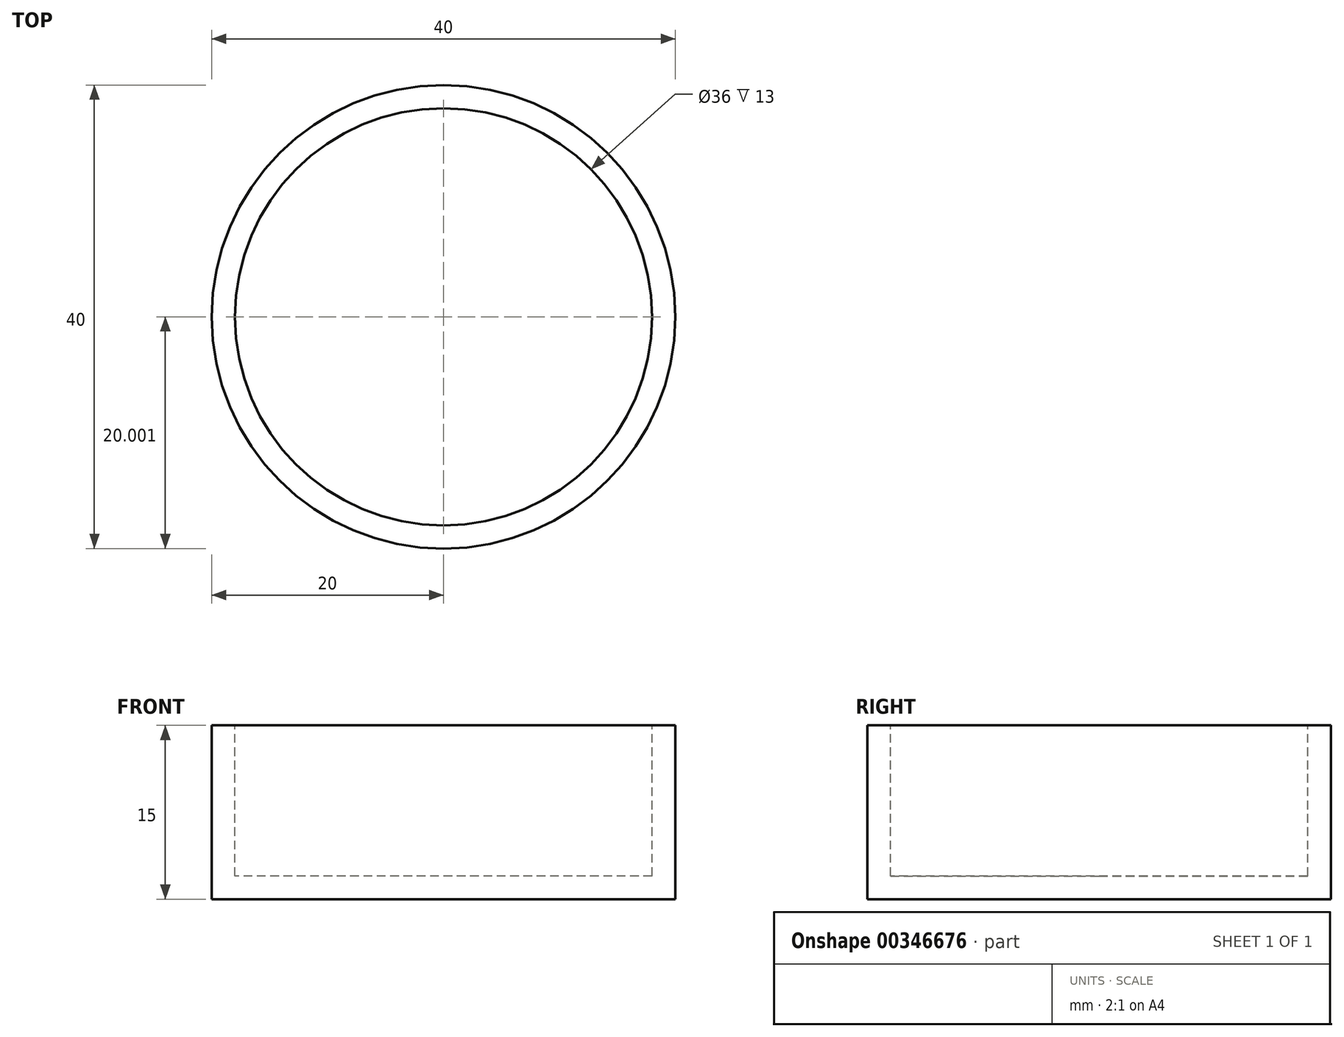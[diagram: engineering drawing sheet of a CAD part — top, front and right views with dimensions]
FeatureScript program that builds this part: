
annotation { "Feature Type Name" : "Feature", "Feature Type Description" : "" }
export const myFeature = defineFeature(function(context is Context, id is Id, definition is map)
    precondition{}
    {
        {
            var Q0;
            Q0=qCreatedBy(makeId("Top.planeOp"),FACE);
            var sketch = newSketch(context, id + "F0", { "sketchPlane" : qUnion([Q0])});
            skCircle(sketch, "E0", {"center": v(0, -2.77) * mm, "radius": 20 * mm});
            skSolve(sketch);
        }
        {
            var Q0;
            Q0=makeQuery(id+"F0.imprint","IMPRINT",FACE,{"disambiguationData":[TD([[makeQuery(id+"F0.imprint","IMPRINT",EDGE,{"derivedFrom":sQuery(id+"F0.wireOp",EDGE,"E0")}),1.0]])]});
            extrude(context, id + "F1", {"entities" : qUnion([Q0]), "depth" : 15 * mm});
        }
        {
            var Q0;
            Q0=makeQuery(id+"F1.opExtrude","CAP_FACE",FACE,{"disambiguationData":[OSD([sQuery(id+"F0.wireOp",EDGE,"E0")])],"isStart":false});
            var sketch = newSketch(context, id + "F2", { "sketchPlane" : qUnion([Q0])});
            skCircle(sketch, "E1", {"center": v(0, -2.77) * mm, "radius": 18 * mm});
            skSolve(sketch);
        }
        {
            var Q0;
            Q0=makeQuery(id+"F2.imprint","IMPRINT",FACE,{"disambiguationData":[TD([[makeQuery(id+"F2.imprint","IMPRINT",EDGE,{"derivedFrom":sQuery(id+"F2.wireOp",EDGE,"E1")}),1.0]])]});
            extrude(context, id + "F3", {"entities" : qUnion([Q0]), "operationType" : NewBodyOperationType.REMOVE, "oppositeDirection" : true, "depth" : 13 * mm});
        }
        {
            var Q0;
            Q0=makeQuery(id+"F3.boolean.opBoolean","COPY",FACE,{"derivedFrom":makeQuery(id+"F3.opExtrude","CAP_FACE",FACE,{"disambiguationData":[OSD([sQuery(id+"F2.wireOp",EDGE,"E1")])],"isStart":false})});
            var sketch = newSketch(context, id + "F4", { "sketchPlane" : qUnion([Q0])});
            skCircle(sketch, "E2", {"center": v(0, -2.77) * mm, "radius": 3.5 * mm});
            skSolve(sketch);
        }
        {
            var Q0;
            Q0=sQuery(id+"F4.wireOp",EDGE,"E2");
            extrude(context, id + "F5", {"bodyType" : ToolBodyType.SURFACE, "surfaceEntities" : qUnion([Q0]), "depth" : 15 * mm});
        }
    });
